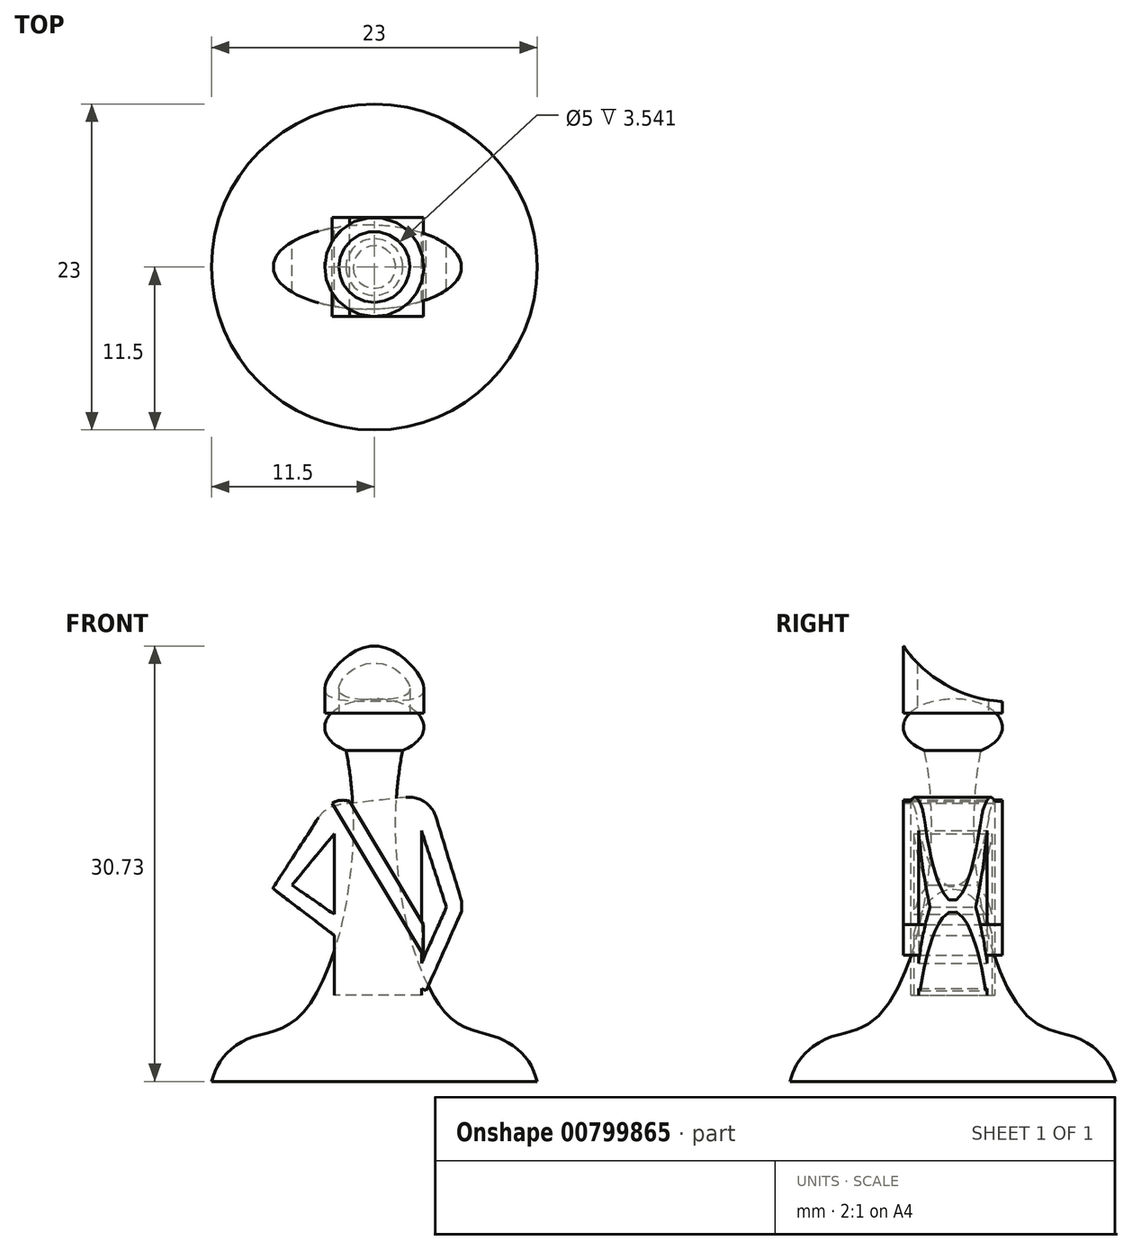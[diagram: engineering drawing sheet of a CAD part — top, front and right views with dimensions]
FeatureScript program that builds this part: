
annotation { "Feature Type Name" : "Feature", "Feature Type Description" : "" }
export const myFeature = defineFeature(function(context is Context, id is Id, definition is map)
    precondition{}
    {
        {
            var Q0;
            Q0=qCreatedBy(makeId("Front.planeOp"),FACE);
            var sketch = newSketch(context, id + "F0", { "sketchPlane" : qUnion([Q0])});
            skLineSegment(sketch, "E0", {"start": v(0, 0) * mm, "end": v(0, 27) * mm});
            skEllipticalArc(sketch, "E1", {});
            skLineSegment(sketch, "E2", {"start": v(0, 0) * mm, "end": v(11.5, 0) * mm});
            skLineSegment(sketch, "E3.0", {"start": v(2, 0) * mm, "end": v(2, 25) * mm, "construction": true});
            skFitSpline(sketch, "E4", {"points": [v(2, 23.36) * mm, v(5.13, 4.74) * mm, v(8.7, 3.1) * mm, v(10.7, 1.65) * mm, v(11.5, 0) * mm], "startDerivative": vector(-9.39, -46.18) * mm, "endDerivative": vector(3.99, -13.24) * mm});
            const initialGuessF0  = {"E1": [0, 0.025, 1, 0, 0.0035, 0.002, 5.3206345592948985, 1.5707963267948966]};
            skSetInitialGuess(sketch, initialGuessF0);
            skSolve(sketch);
        }
        {
            var Q0;
            Q0=makeQuery(id+"F0.imprint","IMPRINT",FACE,{"disambiguationData":[TD([[makeQuery(id+"F0.imprint","IMPRINT",EDGE,{"derivedFrom":sQuery(id+"F0.wireOp",EDGE,"E0")}),-1.0]])]});
            var Q1;
            Q1=sQuery(id+"F0.wireOp",EDGE,"E0");
            revolve(context, id + "F1", {"entities" : qUnion([Q0]), "axis" : qUnion([Q1]), "revolveType" : RevolveType.FULL});
        }
        {
            var Q0;
            Q0=qCreatedBy(makeId("Top.planeOp"),FACE);
            var sketch = newSketch(context, id + "F2", { "sketchPlane" : qUnion([Q0])});
            skCircle(sketch, "E5", {"center": v(0, 0) * mm, "radius": 3.5 * mm});
            skCircle(sketch, "E6.0", {"center": v(0, 0) * mm, "radius": 2.5 * mm});
            skSolve(sketch);
        }
        {
            var Q0;
            Q0=makeQuery(id+"F2.imprint","IMPRINT",FACE,{"disambiguationData":[TD([[makeQuery(id+"F2.imprint","IMPRINT",EDGE,{"derivedFrom":sQuery(id+"F2.wireOp",EDGE,"E5")}),1.0]])]});
            extrude(context, id + "F3", {"entities" : qUnion([Q0]), "depth" : 5 * mm, "offsetDistance" : 25 * mm});
        }
        {
            var Q0;
            Q0=qCreatedBy(makeId("Right.planeOp"),FACE);
            var sketch = newSketch(context, id + "F4", { "sketchPlane" : qUnion([Q0])});
            skCircle(sketch, "E7", {"center": v(4.1, 10.08) * mm, "radius": 9.28 * mm});
            skSolve(sketch);
        }
        {
            var Q0;
            Q0=makeQuery(id+"F4.imprint","IMPRINT",FACE,{"disambiguationData":[TD([[makeQuery(id+"F4.imprint","IMPRINT",EDGE,{"derivedFrom":sQuery(id+"F4.wireOp",EDGE,"E7")}),1.0]])]});
            var Q1;
            Q1=sQuery(id+"F4.wireOp",EDGE,"E7");
            extrude(context, id + "F5", {"entities" : qUnion([Q0]), "surfaceEntities" : qUnion([Q1]), "endBound" : BoundingType.SYMMETRIC, "depth" : 25 * mm, "offsetDistance" : 25 * mm});
        }
        {
            var Q0;
            Q0=makeQuery(id+"F5.opExtrude","SWEPT_BODY",BODY,{"disambiguationData":[OSD([sQuery(id+"F4.wireOp",EDGE,"E7")])]});
            var Q1;
            Q1=makeQuery(id+"F3.opExtrude","SWEPT_BODY",BODY,{"disambiguationData":[OSD([sQuery(id+"F2.wireOp",EDGE,"E5"),sQuery(id+"F2.wireOp",EDGE,"E6.0")])]});
            booleanBodies(context, id + "F6", {"operationType" : BooleanOperationType.SUBTRACTION, "tools" : qUnion([Q0]), "targets" : qUnion([Q1])});
        }
        {
            var Q0;
            Q0=makeQuery(id+"F3.opExtrude","SWEPT_BODY",BODY,{"disambiguationData":[OSD([sQuery(id+"F2.wireOp",EDGE,"E5"),sQuery(id+"F2.wireOp",EDGE,"E6.0")])]});
            var Q1;
            Q1=sQuery(id+"F0.wireOp",EDGE,"E0");
            var Q2;
            Q2=sQuery(id+"F0.wireOp",EDGE,"E0");
            transform(context, id + "F7", {"entities" : qUnion([Q0]), "transformType" : TransformType.TRANSLATION_DISTANCE, "transformDirection" : qUnion([Q2]), "distance" : 26 * mm, "makeCopy" : false});
        }
        {
            var Q0;
            Q0=qCreatedBy(makeId("Front.planeOp"),FACE);
            var sketch = newSketch(context, id + "F8", { "sketchPlane" : qUnion([Q0])});
            skLineSegment(sketch, "E8", {"start": v(-2.47, 19.54) * mm, "end": v(2.22, 20.05) * mm});
            skLineSegment(sketch, "E9", {"start": v(4.35, 18.65) * mm, "end": v(6.3, 12.3) * mm});
            skLineSegment(sketch, "E10", {"start": v(6.3, 12.3) * mm, "end": v(3.66, 6.4) * mm});
            skLineSegment(sketch, "E11", {"start": v(3.66, 6.4) * mm, "end": v(2.66, 6.85) * mm});
            skLineSegment(sketch, "E12", {"start": v(2.66, 6.85) * mm, "end": v(5.1, 12.3) * mm});
            skLineSegment(sketch, "E13", {"start": v(5.1, 12.3) * mm, "end": v(3.33, 17.7) * mm});
            skLineSegment(sketch, "E14", {"start": v(3.33, 17.7) * mm, "end": v(3.33, 6.1) * mm});
            skLineSegment(sketch, "E15", {"start": v(3.33, 6.1) * mm, "end": v(-2.82, 6.1) * mm});
            skLineSegment(sketch, "E16", {"start": v(-2.82, 6.1) * mm, "end": v(-2.82, 10.3) * mm});
            skLineSegment(sketch, "E17", {"start": v(-2.82, 17.48) * mm, "end": v(-5.82, 13.86) * mm});
            skLineSegment(sketch, "E18", {"start": v(-5.82, 13.86) * mm, "end": v(-2.82, 11.79) * mm});
            skLineSegment(sketch, "E19", {"start": v(-2.82, 10.3) * mm, "end": v(-7.18, 13.62) * mm});
            skLineSegment(sketch, "E20", {"start": v(-7.18, 13.62) * mm, "end": v(-3.92, 18.64) * mm});
            skLineSegment(sketch, "E21.trimOffspring", {"start": v(-2.82, 11.79) * mm, "end": v(-2.82, 17.48) * mm});
            skPoint(sketch, "E22.visualSharp", {"position": v(3.87, 20.23) * mm});
            skArc(sketch, "E22.filletArc", {"start": v(4.35, 18.65) * mm, "mid": v(3.54, 19.74) * mm, "end": v(2.22, 20.05) * mm});
            skPoint(sketch, "E23.visualSharp", {"position": v(-3.4, 19.43) * mm});
            skArc(sketch, "E23.filletArc", {"start": v(-2.47, 19.54) * mm, "mid": v(-3.3, 19.25) * mm, "end": v(-3.92, 18.64) * mm});
            skSolve(sketch);
        }
        {
            var Q0;
            Q0 = qSketchRegion(id + "F8", true);
            extrude(context, id + "F9", {"entities" : qUnion([Q0]), "endBound" : BoundingType.SYMMETRIC, "depth" : 6 * mm, "offsetDistance" : 25 * mm});
        }
        {
            var Q0;
            Q0=qCreatedBy(makeId("Top.planeOp"),FACE);
            var sketch = newSketch(context, id + "F10", { "sketchPlane" : qUnion([Q0])});
            skEllipse(sketch, "E24", {"center": v(-0.49, 0) * mm, "majorRadius": 6.65 * mm, "minorRadius": 2.96 * mm, "majorAxis": v(-1, 0)});
            skSolve(sketch);
        }
        {
            var Q0;
            Q0 = qSketchRegion(id + "F10", true);
            extrude(context, id + "F11", {"entities" : qUnion([Q0]), "depth" : 25 * mm, "offsetDistance" : 25 * mm});
        }
        {
            var Q0;
            Q0=makeQuery(id+"F11.opExtrude","SWEPT_BODY",BODY,{"disambiguationData":[OSD([sQuery(id+"F10.wireOp",EDGE,"E24")])]});
            var Q1;
            Q1=makeQuery(id+"F9.opExtrude","SWEPT_BODY",BODY,{"disambiguationData":[OSD([sQuery(id+"F8.wireOp",EDGE,"E8"),sQuery(id+"F8.wireOp",EDGE,"E9"),sQuery(id+"F8.wireOp",EDGE,"E10"),sQuery(id+"F8.wireOp",EDGE,"E11"),sQuery(id+"F8.wireOp",EDGE,"E12"),sQuery(id+"F8.wireOp",EDGE,"E13"),sQuery(id+"F8.wireOp",EDGE,"E14"),sQuery(id+"F8.wireOp",EDGE,"E15"),sQuery(id+"F8.wireOp",EDGE,"E16"),sQuery(id+"F8.wireOp",EDGE,"E17"),sQuery(id+"F8.wireOp",EDGE,"E18"),sQuery(id+"F8.wireOp",EDGE,"E19"),sQuery(id+"F8.wireOp",EDGE,"E20"),sQuery(id+"F8.wireOp",EDGE,"E21.trimOffspring"),sQuery(id+"F8.wireOp",EDGE,"E22.filletArc"),sQuery(id+"F8.wireOp",EDGE,"E23.filletArc")])]});
            booleanBodies(context, id + "F12", {"operationType" : BooleanOperationType.INTERSECTION, "tools" : qUnion([Q0, Q1])});
        }
        {
            var Q0;
            Q0=qCreatedBy(makeId("Front.planeOp"),FACE);
            var sketch = newSketch(context, id + "F13", { "sketchPlane" : qUnion([Q0])});
            skLineSegment(sketch, "E25", {"start": v(-1.74, 19.77) * mm, "end": v(3.45, 11.06) * mm});
            skLineSegment(sketch, "E26", {"start": v(3.45, 11.06) * mm, "end": v(3.45, 8.9) * mm});
            skLineSegment(sketch, "E27", {"start": v(3.45, 8.9) * mm, "end": v(-3, 19.65) * mm});
            skArc(sketch, "E28", {"start": v(-1.74, 19.77) * mm, "mid": v(-2.38, 19.84) * mm, "end": v(-3, 19.65) * mm});
            skSolve(sketch);
        }
        {
            var Q0;
            Q0 = qSketchRegion(id + "F13", true);
            extrude(context, id + "F14", {"entities" : qUnion([Q0]), "endBound" : BoundingType.SYMMETRIC, "depth" : 7 * mm, "offsetDistance" : 25 * mm});
        }
    });
